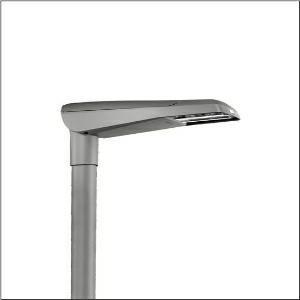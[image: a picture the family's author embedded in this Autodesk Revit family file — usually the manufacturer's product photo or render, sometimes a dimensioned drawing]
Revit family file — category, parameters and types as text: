
# Revit family: streetlight_sl_11_iq_micro___p1_0a_5xc1c41e08ce_7fd7
name_source: partatom
category: Lighting Fixtures
units: mm (PartAtom-declared; Revit-internal decimal feet)

## family parameters
Cut with Voids When Loaded = No
Host = Face
Light Source = No
Part Type = Normal
Room Calculation Point = No
Round Connector Dimension = Use Diameter
Shared = No

## types (1)
- --- (1 x LED, 1660 lm, 10.8 W, 4000K)
    Apparent Load = 11 VA
    CIE Flux Codes = 29 63 93 100 100
    Color Rendering = 70
    Color Temperature = 4000K
    Default Elevation = 1800 mm
    Description = Streetlight SL 11 iQ micro, mast luminaire, primary light control with 3 zone facetted reflector, of plastic, silver coated, highly specular, primary optical cover: cover, of PMMA, transparent, light distribution: P1.0a, light emission: direct distribution, primary light characteristic: asymmetric, installation type: post-top, side-entry, lamps: LED, High Power LED, rated values: 1.660lm | 10,8W | 153,7lm/W (begin service life); end service life: 1.660lm | 11,1W; at 50% lumin. flux: 830lm | 6W | 138,3lm/W, colour temperature: 4000K, colour rendering: CRI > 70, light colour: 740, light setting 1 begin service life: 100% | 1.660lm | 10,8W | 153,7lm/W | 4.000K, light setting 1 end service life: 11,1W, further light settings possible, control: optimised constant luminous flux control (CLO 2.0), Desk-Remote (wireless, voltage-free reading and setting of iQ features in the workshop via application-optimized NFC function/RFID function), Light-Fading, Smart-Wire, Night-Set, Lumen-Switch, Temp-Guard, Auto-Match, with cable H07RN-F 5x 1.5mm², mains connection: 230..240V, AC, 50/60Hz, connection cable pre-assembled, cable length: 5,5m, luminaire housing, of diecast aluminium, powder-coated, Siteco® metallic grey (DB 702S), please order mast flange separately, inclination adjustable without tools: 0°, 5°, 10°, 15° (post-top) | 0°, -5°, -10°, -15° (side-entry), sealing non-destructively replaceable, multi-level sealing system, length: 600mm, width: 174mm, height: 116mm, mast flange for spigot size: 42mm (side-entry): 5XC10008XM4, 60/48mm (side-entry/post-top): 5XC10108XM2, 76/60mm (side-entry/post-top): 5XC10108XM1, equipment: standard, protection rating (complete): IP66, insulation class (complete): insulation class II (safety insulation), certification: CE, ENEC, ENEC+, VDE, impact resistance: IK10, permissible operating ambient temperature for outdoor applications: -25..+50°C, standard-compliant lighting for roads and squares, Environmental Product Declaration (EPD) tested and certified by an independent institute, packaging unit: 1 piece

Light Distribution: P1.0a
    Height = 116 mm
    Lamp = 1 x LED
    Lamp Light Flux = 1660 lm
    Lamp Power = 10.8 W
    Lamp count = 1
    Length = 600 mm
    Luminous efficacy = 154 lm/W
    Manufacturer = Siteco
    ModVariant = No
    Model = 5XC1C41E08CE
    Number of Poles = 1
    OnlyDefault = Yes
    Power Factor = 1
    Product Name = Streetlight SL 11 iQ micro | P1.0a
    Product group = mast luminaire | pylon top
    ProductGroupID = 6100
    Protection Class = Protection class II
    Protection Degree = IP 66
    RLX_Detail_Level = 1
    RLX_Emergency_Light_Flux = 0 lm
    RLX_Emergency_Type = 0
    RLX_Emergency_Type_DB = No
    RlxData = <blob elided: 26649 chars, md5=315e03cf>
    Socket = socket
    Standby Power = 0 W
    System Light Flux = 1660 lm
    System Power = 11 W
    Type Comments = factory setting: luminous flux: 100 % | dim-lin: 254 | 194 mA
    Type Image = l_1006566.jpg
    URL = http://relux.com
    VarID = @adj_018245
    Voltage = 0 V
    Weight = 0.00 kg
    Width = 174 mm

## geometry (parser evidence)
native form markers: Blend x4, Sweep x10
no freeform markers — native parametric forms only
